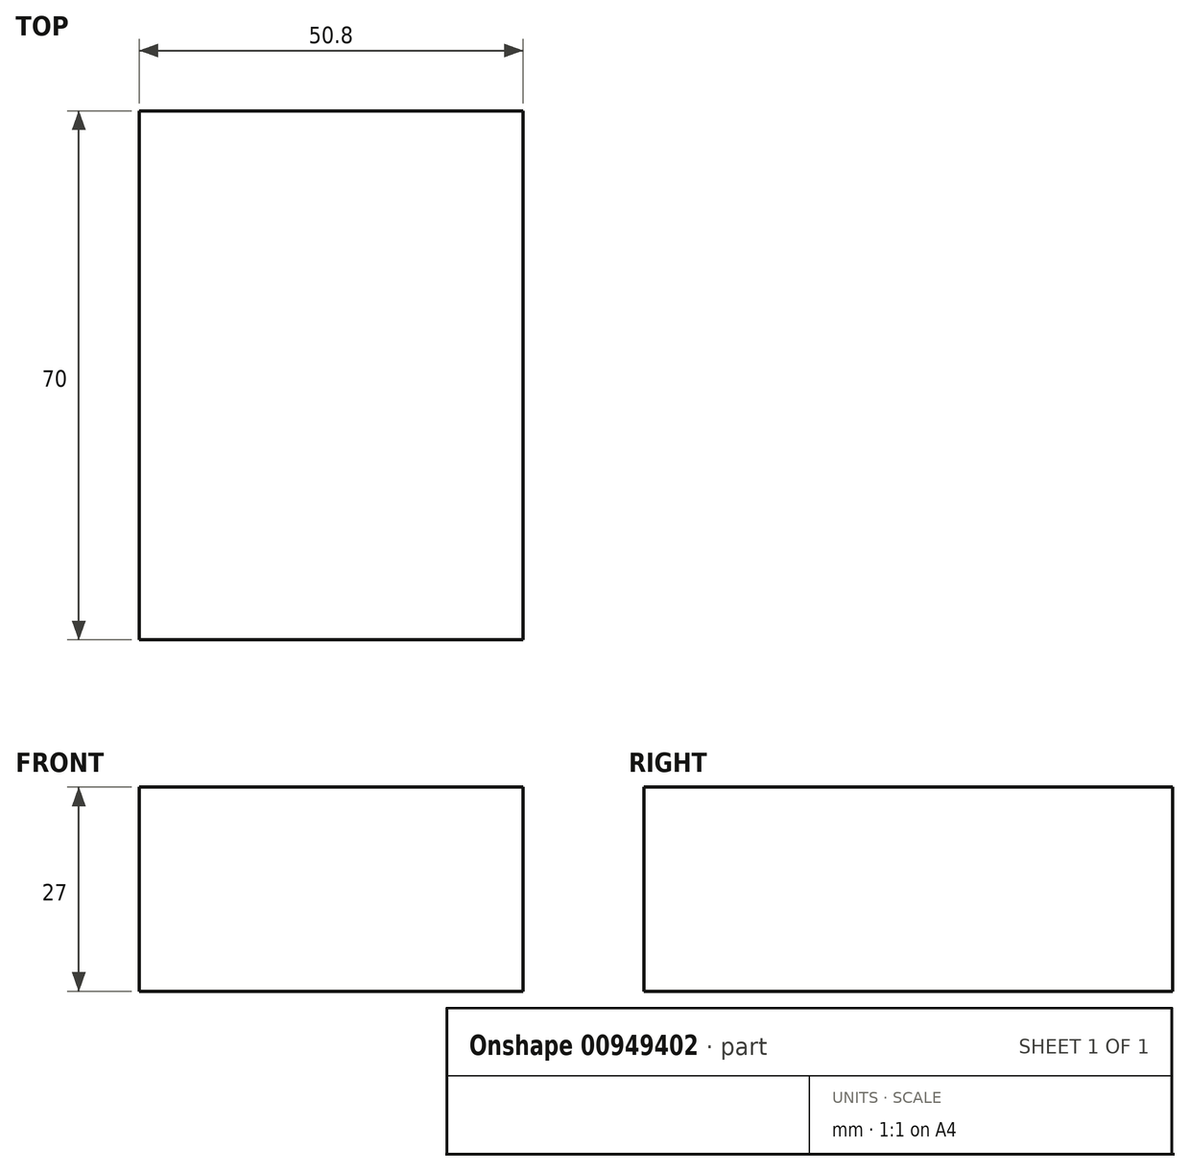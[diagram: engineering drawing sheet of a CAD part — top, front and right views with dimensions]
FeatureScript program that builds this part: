
annotation { "Feature Type Name" : "Feature", "Feature Type Description" : "" }
export const myFeature = defineFeature(function(context is Context, id is Id, definition is map)
    precondition{}
    {
        {
            var Q0;
            Q0=qCreatedBy(makeId("Top.planeOp"),FACE);
            var sketch = newSketch(context, id + "F0", { "sketchPlane" : qUnion([Q0])});
            skLineSegment(sketch, "E0.bottom", {"start": v(25.4, -35) * mm, "end": v(-25.4, -35) * mm});
            skLineSegment(sketch, "E0.top", {"start": v(25.4, 35) * mm, "end": v(-25.4, 35) * mm});
            skLineSegment(sketch, "E0.left", {"start": v(25.4, -35) * mm, "end": v(25.4, 35) * mm});
            skLineSegment(sketch, "E0.right", {"start": v(-25.4, -35) * mm, "end": v(-25.4, 35) * mm});
            skPoint(sketch, "E0.middle", {"position": v(0, 0) * mm});
            skSolve(sketch);
        }
        {
            var Q0;
            Q0 = qSketchRegion(id + "F0", true);
            extrude(context, id + "F1", {"entities" : qUnion([Q0]), "depth" : 27 * mm, "offsetDistance" : 25.4 * mm});
        }
    });
